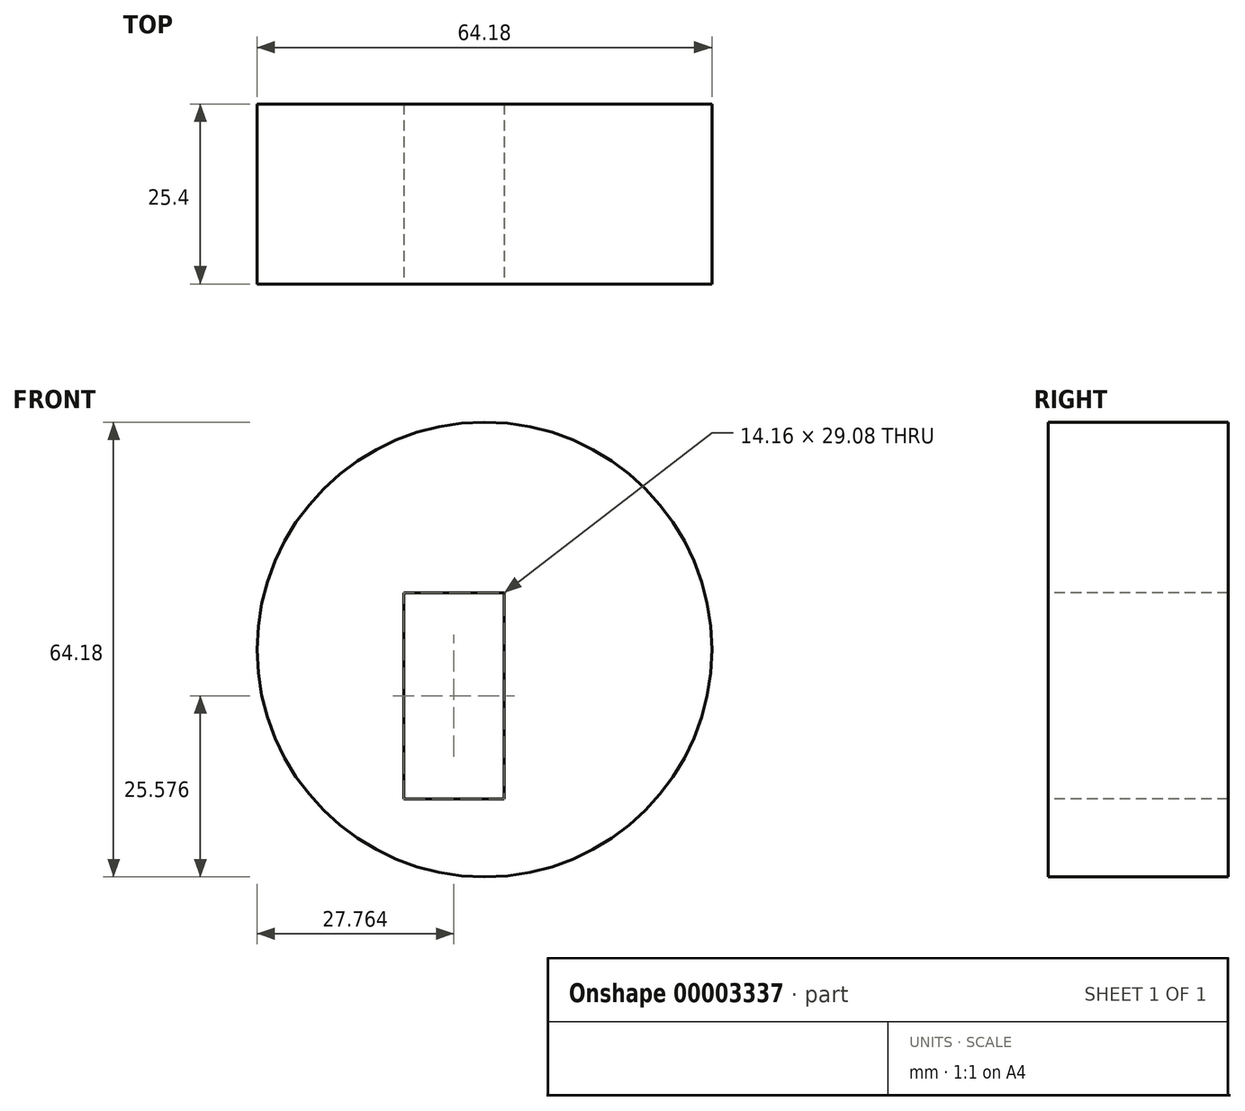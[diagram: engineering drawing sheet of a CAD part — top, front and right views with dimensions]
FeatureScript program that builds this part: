
annotation { "Feature Type Name" : "Feature", "Feature Type Description" : "" }
export const myFeature = defineFeature(function(context is Context, id is Id, definition is map)
    precondition{}
    {
        {
            var Q0;
            Q0=qCreatedBy(makeId("Front.planeOp"),FACE);
            var sketch = newSketch(context, id + "F0", { "sketchPlane" : qUnion([Q0])});
            skCircle(sketch, "E0", {"center": v(0, 0) * mm, "radius": 32.09 * mm});
            skSolve(sketch);
        }
        {
            var Q0;
            Q0=makeQuery(id+"F0.imprint","IMPRINT",FACE,{"disambiguationData":[TD([[makeQuery(id+"F0.imprint","IMPRINT",EDGE,{"derivedFrom":sQuery(id+"F0.wireOp",EDGE,"E0")}),1.0]])]});
            extrude(context, id + "F1", {"entities" : qUnion([Q0]), "depth" : 25.4 * mm});
        }
        {
            var Q0;
            Q0=makeQuery(id+"F1.opExtrude","CAP_FACE",FACE,{"disambiguationData":[OSD([sQuery(id+"F0.wireOp",EDGE,"E0")])],"isStart":false});
            var sketch = newSketch(context, id + "F2", { "sketchPlane" : qUnion([Q0])});
            skLineSegment(sketch, "E1.bottom", {"start": v(-11.4, 8.03) * mm, "end": v(2.75, 8.03) * mm});
            skLineSegment(sketch, "E1.top", {"start": v(-11.4, -21.06) * mm, "end": v(2.75, -21.06) * mm});
            skLineSegment(sketch, "E1.left", {"start": v(-11.4, 8.03) * mm, "end": v(-11.4, -21.06) * mm});
            skLineSegment(sketch, "E1.right", {"start": v(2.75, 8.03) * mm, "end": v(2.75, -21.06) * mm});
            skSolve(sketch);
        }
        {
            var Q0;
            Q0=makeQuery(id+"F2.imprint","IMPRINT",FACE,{"disambiguationData":[TD([[makeQuery(id+"F2.imprint","IMPRINT",EDGE,{"derivedFrom":sQuery(id+"F2.wireOp",EDGE,"E1.bottom")}),-1.0]])]});
            extrude(context, id + "F3", {"entities" : qUnion([Q0]), "operationType" : NewBodyOperationType.REMOVE, "endBound" : BoundingType.UP_TO_NEXT, "oppositeDirection" : true, "depth" : 43.07 * mm});
        }
    });
